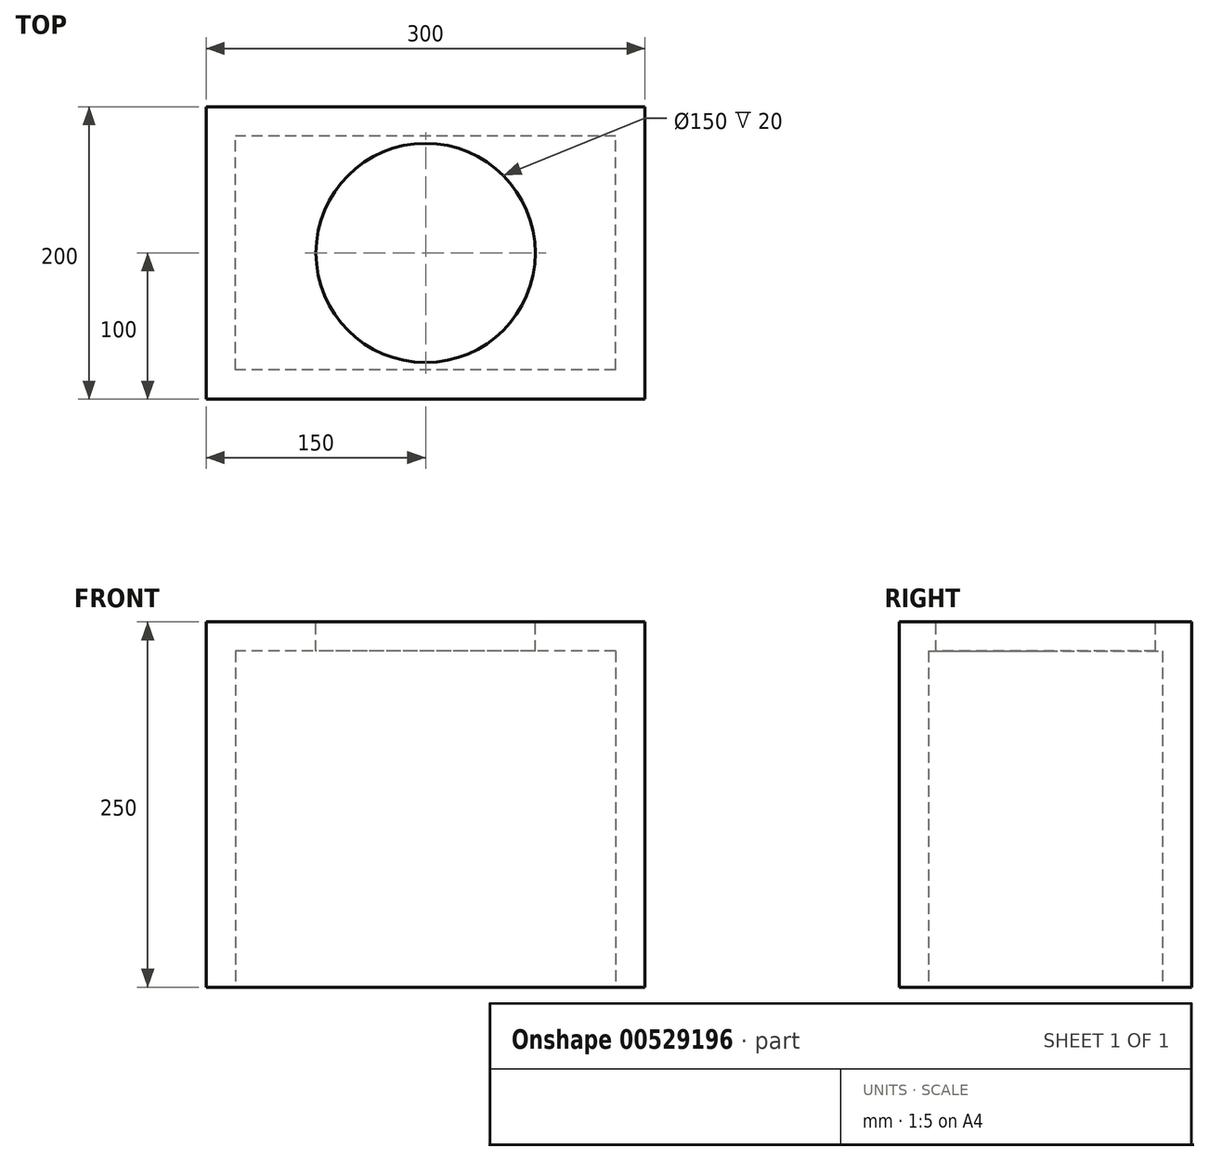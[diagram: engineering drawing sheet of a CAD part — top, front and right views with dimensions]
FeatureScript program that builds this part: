
annotation { "Feature Type Name" : "Feature", "Feature Type Description" : "" }
export const myFeature = defineFeature(function(context is Context, id is Id, definition is map)
    precondition{}
    {
        {
            var Q0;
            Q0=qCreatedBy(makeId("Top.planeOp"),FACE);
            var sketch = newSketch(context, id + "F0", { "sketchPlane" : qUnion([Q0])});
            skLineSegment(sketch, "E0.bottom", {"start": v(150, -100) * mm, "end": v(-150, -100) * mm});
            skLineSegment(sketch, "E0.top", {"start": v(150, 100) * mm, "end": v(-150, 100) * mm});
            skLineSegment(sketch, "E0.left", {"start": v(150, -100) * mm, "end": v(150, 100) * mm});
            skLineSegment(sketch, "E0.right", {"start": v(-150, -100) * mm, "end": v(-150, 100) * mm});
            skPoint(sketch, "E0.middle", {"position": v(0, 0) * mm});
            skSolve(sketch);
        }
        {
            var Q0;
            Q0=makeQuery(id+"F0.imprint","IMPRINT",FACE,{"disambiguationData":[TD([[makeQuery(id+"F0.imprint","IMPRINT",EDGE,{"derivedFrom":sQuery(id+"F0.wireOp",EDGE,"E0.bottom")}),-1.0]])]});
            extrude(context, id + "F1", {"entities" : qUnion([Q0]), "depth" : 250 * mm, "offsetDistance" : 25 * mm});
        }
        {
            var Q0;
            Q0=makeQuery(id+"F1.opExtrude","CAP_FACE",FACE,{"disambiguationData":[OSD([sQuery(id+"F0.wireOp",EDGE,"E0.bottom"),sQuery(id+"F0.wireOp",EDGE,"E0.top"),sQuery(id+"F0.wireOp",EDGE,"E0.left"),sQuery(id+"F0.wireOp",EDGE,"E0.right")])],"isStart":false});
            var sketch = newSketch(context, id + "F2", { "sketchPlane" : qUnion([Q0])});
            skCircle(sketch, "E1", {"center": v(0, 0) * mm, "radius": 75 * mm});
            skSolve(sketch);
        }
        {
            var Q0;
            Q0=makeQuery(id+"F1.opExtrude","CAP_FACE",FACE,{"disambiguationData":[OSD([sQuery(id+"F0.wireOp",EDGE,"E0.bottom"),sQuery(id+"F0.wireOp",EDGE,"E0.top"),sQuery(id+"F0.wireOp",EDGE,"E0.left"),sQuery(id+"F0.wireOp",EDGE,"E0.right")])],"isStart":true});
            shell(context, id + "F3", {"entities" : qUnion([Q0]), "thickness" : 20 * mm});
        }
        {
            var Q0;
            Q0=sQuery(id+"F2.wireOp",VERTEX,"E1.center");
            var Q1;
            Q1=makeQuery(id+"F1.opExtrude","SWEPT_BODY",BODY,{"disambiguationData":[OSD([sQuery(id+"F0.wireOp",EDGE,"E0.bottom"),sQuery(id+"F0.wireOp",EDGE,"E0.top"),sQuery(id+"F0.wireOp",EDGE,"E0.left"),sQuery(id+"F0.wireOp",EDGE,"E0.right")])]});
            hole(context, id + "F4", {"style" : HoleStyle.SIMPLE, "endStyle" : HoleEndStyle.THROUGH, "holeDiameter" : 150 * mm, "isTappedThrough" : true, "tappedDepth" : 12 * mm, "tapClearance" : 3, "locations" : qUnion([Q0]), "scope" : qUnion([Q1])});
        }
    });
